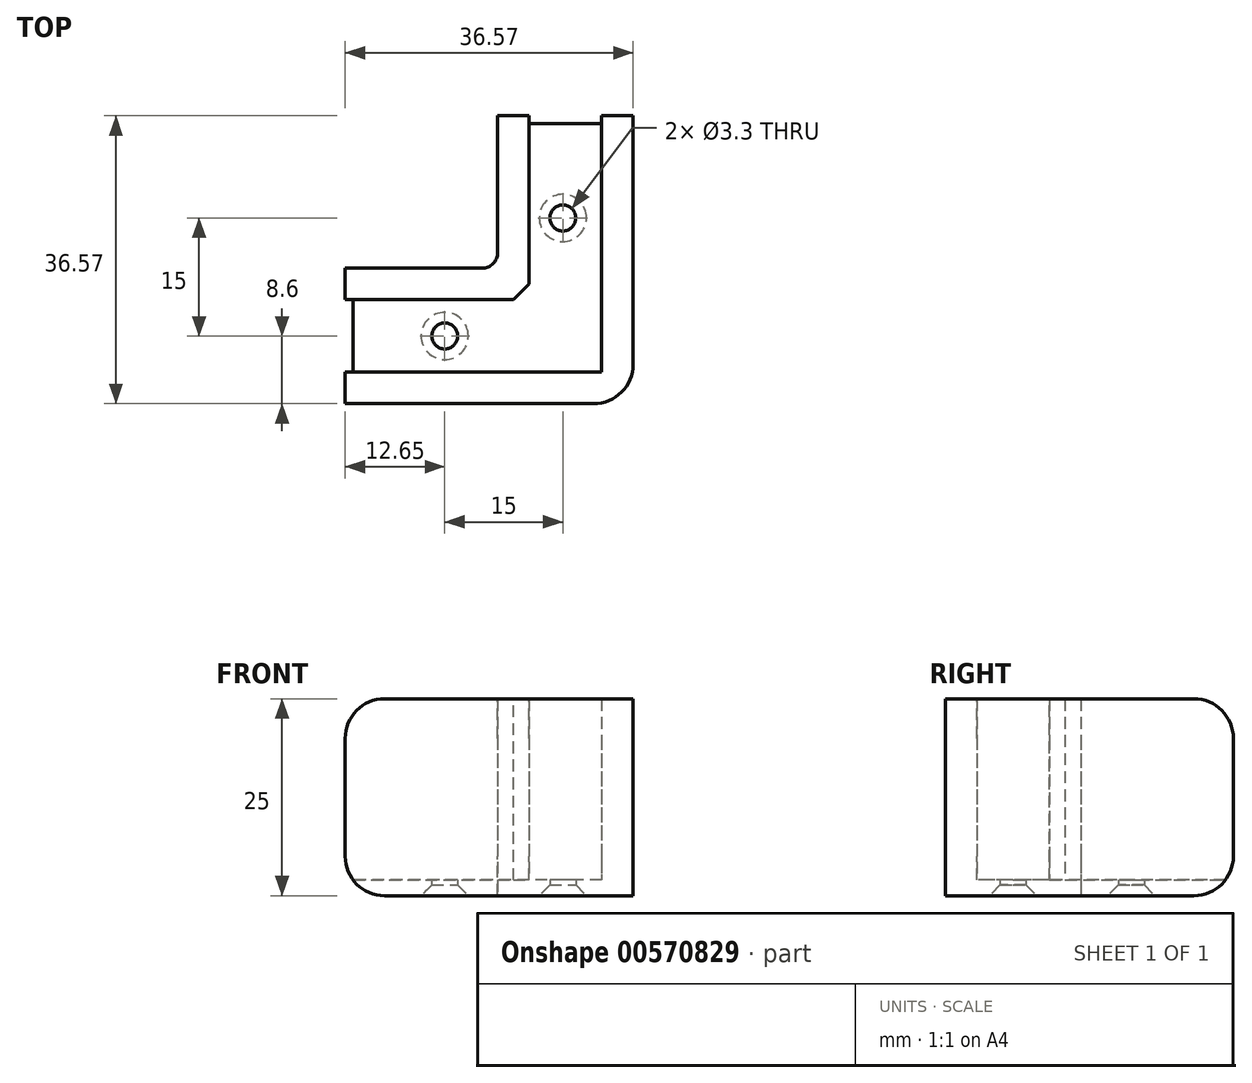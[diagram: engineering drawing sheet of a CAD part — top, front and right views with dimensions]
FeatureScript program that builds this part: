
annotation { "Feature Type Name" : "Feature", "Feature Type Description" : "" }
export const myFeature = defineFeature(function(context is Context, id is Id, definition is map)
    precondition{}
    {
        {
            var Q0;
            Q0=qCreatedBy(makeId("Top.planeOp"),FACE);
            var sketch = newSketch(context, id + "F0", { "sketchPlane" : qUnion([Q0])});
            skLineSegment(sketch, "E0", {"start": v(4.92, 9.2) * mm, "end": v(4.92, 32.57) * mm});
            skLineSegment(sketch, "E1", {"start": v(-4.28, 32.57) * mm, "end": v(-4.28, 9.2) * mm});
            skLineSegment(sketch, "E2", {"start": v(-4.28, 9.2) * mm, "end": v(-27.65, 9.2) * mm});
            skLineSegment(sketch, "E3", {"start": v(-27.65, 0) * mm, "end": v(0, 0) * mm});
            skLineSegment(sketch, "E4.0", {"start": v(8.92, 32.57) * mm, "end": v(-8.28, 32.57) * mm});
            skLineSegment(sketch, "E4.2", {"start": v(-8.28, 32.57) * mm, "end": v(-8.28, 13.2) * mm});
            skLineSegment(sketch, "E4.5", {"start": v(-8.28, 13.2) * mm, "end": v(-27.65, 13.2) * mm});
            skLineSegment(sketch, "E4.6", {"start": v(-27.65, 13.2) * mm, "end": v(-27.65, -4) * mm});
            skLineSegment(sketch, "E4.7", {"start": v(-27.65, -4) * mm, "end": v(0, -4) * mm});
            skLineSegment(sketch, "E5", {"start": v(8.92, 32.57) * mm, "end": v(8.92, -4) * mm});
            skLineSegment(sketch, "E6", {"start": v(0, -4) * mm, "end": v(8.92, -4) * mm});
            skLineSegment(sketch, "E7", {"start": v(0, 0) * mm, "end": v(4.92, 0) * mm});
            skLineSegment(sketch, "E8", {"start": v(4.92, 0) * mm, "end": v(4.92, 9.2) * mm});
            skSolve(sketch);
        }
        {
            var Q0;
            Q0=qSketchRegion(id+"F0",true);
            extrude(context, id + "F1", {"entities" : qUnion([Q0]), "depth" : 2 * mm, "offsetDistance" : 25 * mm});
        }
        {
            var Q0;
            {var subQ3=sQuery(id+"F0.wireOp",EDGE,"E1");Q0=makeQuery(id+"F0.imprint","IMPRINT",FACE,{"disambiguationData":[TD([[makeQuery(id+"F0.imprint","IMPRINT",EDGE,{"derivedFrom":subQ3}),-1.0]])]});}
            var Q1;
            {var subQ3=sQuery(id+"F0.wireOp",EDGE,"E0");Q1=makeQuery(id+"F0.imprint","IMPRINT",FACE,{"disambiguationData":[TD([[makeQuery(id+"F0.imprint","IMPRINT",EDGE,{"derivedFrom":subQ3}),-1.0]])]});}
            extrude(context, id + "F2", {"entities" : qUnion([Q0, Q1]), "operationType" : NewBodyOperationType.ADD, "depth" : 25 * mm, "offsetDistance" : 25 * mm});
        }
        {
            var Q0;
            {var subQ0=sQuery(id+"F0.wireOp",EDGE,"E4.4");Q0=makeQuery(id+"F2.opExtrude","CAP_EDGE",EDGE,{"disambiguationData":[OSD([subQ0]),TDD([makeQuery(id+"F0.imprint","IMPRINT",EDGE,{"disambiguationData":[TD([[makeQuery(id+"F0.imprint","INTERSECT",VERTEX,{"derivedFrom":[sQuery(id+"F0.wireOp",EDGE,"4AKFVKuP-VGzW-Z0gR-biP7-avwRZvC0l9sY"),subQ0]}),1.0]])],"derivedFrom":subQ0})])],"isStart":false});}
            var Q1;
            {var subQ0=sQuery(id+"F0.wireOp",EDGE,"E4.4");Q1=makeQuery(id+"F2.opExtrude","CAP_EDGE",EDGE,{"disambiguationData":[OSD([subQ0]),TDD([makeQuery(id+"F0.imprint","IMPRINT",EDGE,{"disambiguationData":[TD([[makeQuery(id+"F0.imprint","INTERSECT",VERTEX,{"derivedFrom":[sQuery(id+"F0.wireOp",EDGE,"wGMG52vS-Bb6S-6M2K-uLHt-X8AWWQIAXK16"),subQ0]}),-1.0]])],"derivedFrom":subQ0})])],"isStart":false});}
            var Q2;
            {var subQ0=sQuery(id+"F0.wireOp",EDGE,"E4.6");Q2=makeQuery(id+"F2.opExtrude","CAP_EDGE",EDGE,{"disambiguationData":[OSD([subQ0]),TDD([makeQuery(id+"F0.imprint","IMPRINT",EDGE,{"disambiguationData":[TD([[makeQuery(id+"F0.imprint","INTERSECT",VERTEX,{"derivedFrom":[sQuery(id+"F0.wireOp",EDGE,"E3"),subQ0]}),-1.0]])],"derivedFrom":subQ0})])],"isStart":false});}
            var Q3;
            {var subQ0=sQuery(id+"F0.wireOp",EDGE,"E4.6");Q3=makeQuery(id+"F2.opExtrude","CAP_EDGE",EDGE,{"disambiguationData":[OSD([subQ0]),TDD([makeQuery(id+"F0.imprint","IMPRINT",EDGE,{"disambiguationData":[TD([[makeQuery(id+"F0.imprint","INTERSECT",VERTEX,{"derivedFrom":[sQuery(id+"F0.wireOp",EDGE,"E2"),subQ0]}),1.0]])],"derivedFrom":subQ0})])],"isStart":false});}
            var Q4;
            {var subQ0=sQuery(id+"F0.wireOp",EDGE,"E4.0");Q4=makeQuery(id+"F2.opExtrude","CAP_EDGE",EDGE,{"disambiguationData":[OSD([subQ0]),TDD([makeQuery(id+"F0.imprint","IMPRINT",EDGE,{"disambiguationData":[TD([[makeQuery(id+"F0.imprint","INTERSECT",VERTEX,{"derivedFrom":[sQuery(id+"F0.wireOp",EDGE,"E1"),subQ0]}),-1.0]])],"derivedFrom":subQ0})])],"isStart":false});}
            var Q5;
            {var subQ0=sQuery(id+"F0.wireOp",EDGE,"E4.0");Q5=makeQuery(id+"F2.opExtrude","CAP_EDGE",EDGE,{"disambiguationData":[OSD([subQ0]),TDD([makeQuery(id+"F0.imprint","IMPRINT",EDGE,{"disambiguationData":[TD([[makeQuery(id+"F0.imprint","INTERSECT",VERTEX,{"derivedFrom":[sQuery(id+"F0.wireOp",EDGE,"E0"),subQ0]}),1.0]])],"derivedFrom":subQ0})])],"isStart":false});}
            var Q6;
            Q6=makeQuery(id+"F1.opExtrude","CAP_EDGE",EDGE,{"disambiguationData":[OSD([sQuery(id+"F0.wireOp",EDGE,"E4.6")])],"isStart":true});
            var Q7;
            Q7=makeQuery(id+"F1.opExtrude","CAP_EDGE",EDGE,{"disambiguationData":[OSD([sQuery(id+"F0.wireOp",EDGE,"E4.4")])],"isStart":true});
            var Q8;
            Q8=makeQuery(id+"F1.opExtrude","CAP_EDGE",EDGE,{"disambiguationData":[OSD([sQuery(id+"F0.wireOp",EDGE,"E4.0")])],"isStart":true});
            var Q9;
            {var subQ0=sQuery(id+"F0.wireOp",EDGE,"E6");var subQ1=sQuery(id+"F0.wireOp",EDGE,"E5");Q9=makeQuery(id+"F2.boolean.opBoolean","MERGE",EDGE,{"derivedFrom":[makeQuery(id+"F1.opExtrude","SWEPT_EDGE",EDGE,{"disambiguationData":[OSD([subQ1,subQ0])]}),makeQuery(id+"F2.opExtrude","SWEPT_EDGE",EDGE,{"disambiguationData":[OSD([subQ1,subQ0])]})]});}
            fillet(context, id + "F3", {"entities" : qUnion([Q0, Q1, Q2, Q3, Q4, Q5, Q6, Q7, Q8, Q9]), "radius" : 5 * mm, "tangentPropagation" : true, "allowEdgeOverflow" : false});
        }
        {
            var Q0;
            {var subQ0=sQuery(id+"F0.wireOp",EDGE,"E4.5");var subQ1=sQuery(id+"F0.wireOp",EDGE,"E4.2");Q0=makeQuery(id+"F2.boolean.opBoolean","MERGE",EDGE,{"derivedFrom":[makeQuery(id+"F1.opExtrude","SWEPT_EDGE",EDGE,{"disambiguationData":[OSD([subQ1,subQ0])]}),makeQuery(id+"F2.opExtrude","SWEPT_EDGE",EDGE,{"disambiguationData":[OSD([subQ1,subQ0])]})]});}
            fillet(context, id + "F4", {"entities" : qUnion([Q0]), "radius" : 2 * mm, "tangentPropagation" : true, "allowEdgeOverflow" : false});
        }
        {
            var Q0;
            Q0=makeQuery(id+"F2.opExtrude","SWEPT_EDGE",EDGE,{"disambiguationData":[OSD([sQuery(id+"F0.wireOp",EDGE,"E1"),sQuery(id+"F0.wireOp",EDGE,"E2")])]});
            chamfer(context, id + "F5", {"entities" : qUnion([Q0]), "width" : 2 * mm, "tangentPropagation" : true});
        }
        {
            var Q0;
            {var subQ3=sQuery(id+"F0.wireOp",EDGE,"E0");Q0=makeQuery(id+"F0.imprint","IMPRINT",FACE,{"disambiguationData":[TD([[makeQuery(id+"F0.imprint","IMPRINT",EDGE,{"derivedFrom":subQ3}),1.0]])]});}
            var sketch = newSketch(context, id + "F6", { "sketchPlane" : qUnion([Q0])});
            skLineSegment(sketch, "E9", {"start": v(-22.65, 4.6) * mm, "end": v(7.14, 4.6) * mm});
            skPoint(sketch, "E10", {"position": v(-15, 4.6) * mm});
            skPoint(sketch, "E11", {"position": v(0, 19.6) * mm});
            skSolve(sketch);
        }
        {
            var Q0;
            Q0=sQuery(id+"F6.wireOp",VERTEX,"E10");
            var Q1;
            Q1=sQuery(id+"F6.wireOp",VERTEX,"E11");
            var Q2;
            Q2=sQuery(id+"F6.wireOp",VERTEX,"148682fb-4106-4836-a6ce-08a78baf88f0");
            var Q3;
            Q3=makeQuery(id+"F1.opExtrude","SWEPT_BODY",BODY,{"disambiguationData":[OSD([sQuery(id+"F0.wireOp",EDGE,"E4.0"),sQuery(id+"F0.wireOp",EDGE,"E4.1"),sQuery(id+"F0.wireOp",EDGE,"E4.2"),sQuery(id+"F0.wireOp",EDGE,"E4.3"),sQuery(id+"F0.wireOp",EDGE,"E4.4"),sQuery(id+"F0.wireOp",EDGE,"E4.5"),sQuery(id+"F0.wireOp",EDGE,"E4.6"),sQuery(id+"F0.wireOp",EDGE,"E4.7"),sQuery(id+"F0.wireOp",EDGE,"E4.8")])]});
            hole(context, id + "F7", {"style" : HoleStyle.C_SINK, "endStyle" : HoleEndStyle.THROUGH, "oppositeDirection" : true, "holeDiameter" : 3.3 * mm, "cSinkDiameter" : 6 * mm, "cSinkAngle" : 90 * degree, "majorDiameter" : 5 * mm, "isTappedThrough" : true, "tappedDepth" : 12 * mm, "tapClearance" : 3, "locations" : qUnion([Q0, Q1, Q2]), "scope" : qUnion([Q3])});
        }
    });
